# Revit family: 3459A_NX_Daylight_Sensor
name_source: partatom
category: Communication Devices
units: mm (PartAtom-declared; Revit-internal decimal feet)

## family parameters
Cut with Voids When Loaded = No
Host = Face
Maintain Annotation Orientation = No
OmniClass Number = 23.85.80.11.27
OmniClass Title = Lighting Controls
Part Type = Normal
Room Calculation Point = No
Round Connector Dimension = Use Diameter
Shared = Yes

## types (1)
- 3459A_NX_Daylight_Sensor
    Assembly Code = D5090
    Certification = UL and cUL listed
    Default Elevation = 48 "
    Description = key component in a NX Network Lighting Control System, providing programmable switching and dimming control of the projects lighting circuits
    Features = Indoor and Outdoor models available
• Architecturally attractive design
• Open loop operation
• Foot-candle range: 3-6,000fc
• Mounts vertically or horizontally
• Color coded, plug-and-play integration with NX Room Controller
    Housing Material = Glass - White
    Manufacturer = NX Lighting Controls
    Sensing Element = Plastic -  Blue
    Type Comments = NX Daylight Sensor
    URL = https://www.currentlighting.com
    Warranty = 5-Years Warranty

## geometry (parser evidence)
native form markers: Sweep x3
no freeform markers — native parametric forms only
